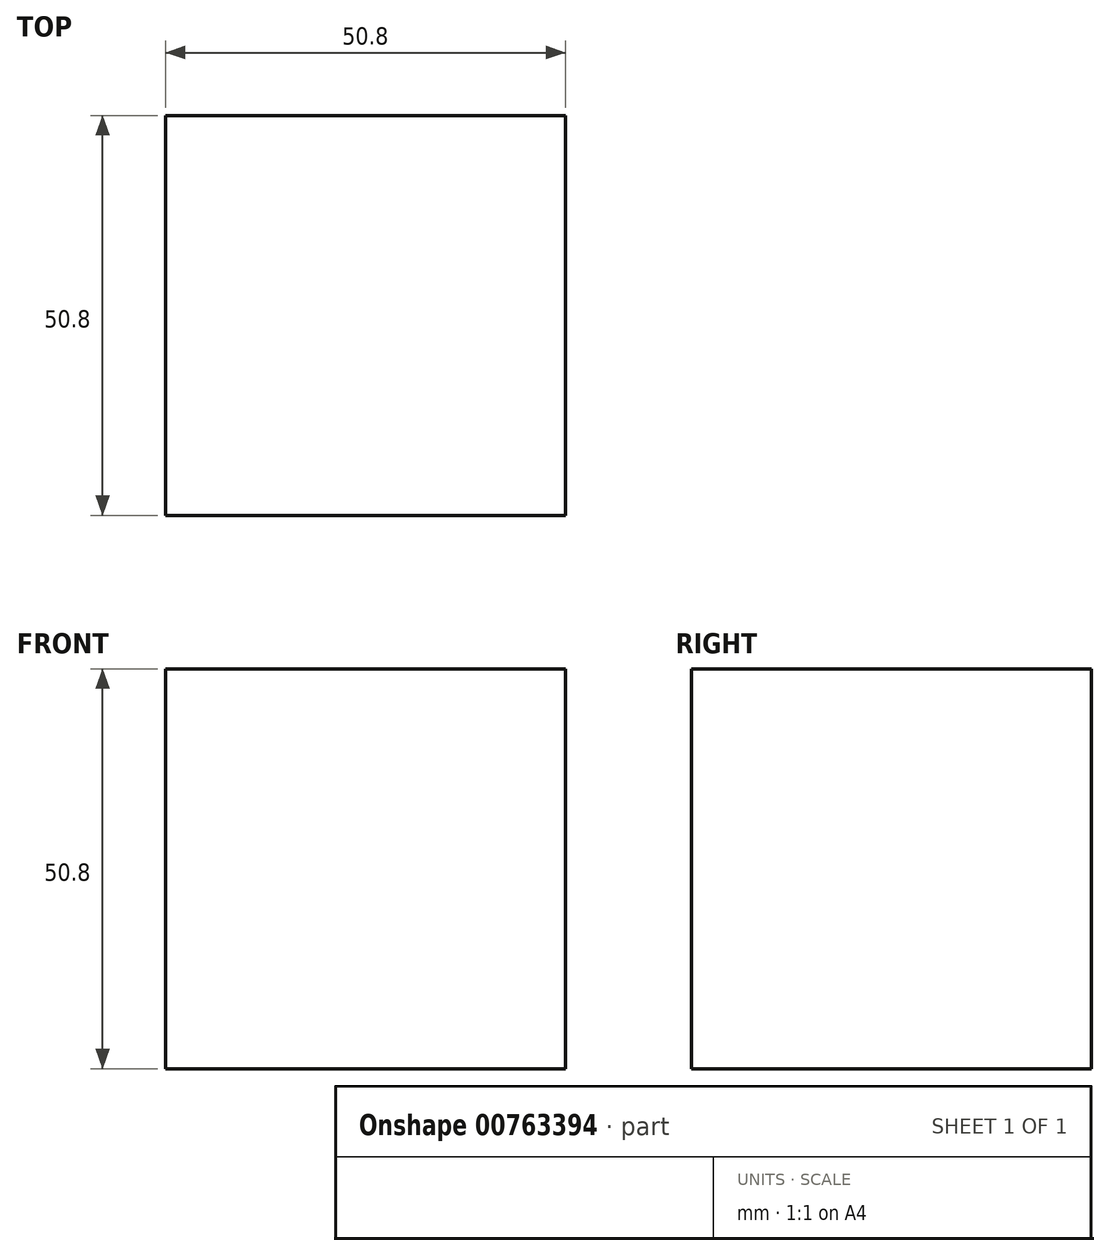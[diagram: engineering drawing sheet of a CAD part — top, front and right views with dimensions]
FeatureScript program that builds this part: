
annotation { "Feature Type Name" : "Feature", "Feature Type Description" : "" }
export const myFeature = defineFeature(function(context is Context, id is Id, definition is map)
    precondition{}
    {
        {
            var Q0;
            Q0=qCreatedBy(makeId("Front.planeOp"),FACE);
            var sketch = newSketch(context, id + "F0", { "sketchPlane" : qUnion([Q0])});
            skLineSegment(sketch, "E0.bottom", {"start": v(-25.4, 25.4) * mm, "end": v(25.4, 25.4) * mm});
            skLineSegment(sketch, "E0.top", {"start": v(-25.4, -25.4) * mm, "end": v(25.4, -25.4) * mm});
            skLineSegment(sketch, "E0.left", {"start": v(-25.4, 25.4) * mm, "end": v(-25.4, -25.4) * mm});
            skLineSegment(sketch, "E0.right", {"start": v(25.4, 25.4) * mm, "end": v(25.4, -25.4) * mm});
            skLineSegment(sketch, "E1", {"start": v(0, 0) * mm, "end": v(25.4, 0) * mm, "construction": true});
            skLineSegment(sketch, "E2", {"start": v(0, 0) * mm, "end": v(0, 25.4) * mm, "construction": true});
            skLineSegment(sketch, "E3", {"start": v(0, 0) * mm, "end": v(-25.4, 0) * mm});
            skLineSegment(sketch, "E4", {"start": v(0, 0) * mm, "end": v(0, -25.4) * mm});
            skSolve(sketch);
        }
        {
            var Q0;
            {var subQ1=sQuery(id+"F0.wireOp",EDGE,"E0.bottom");Q0=makeQuery(id+"F0.imprint","IMPRINT",FACE,{"disambiguationData":[TD([[makeQuery(id+"F0.imprint","IMPRINT",EDGE,{"derivedFrom":subQ1}),-1.0]])]});}
            var Q1;
            {var subQ5=sQuery(id+"F0.wireOp",EDGE,"E3");Q1=makeQuery(id+"F0.imprint","IMPRINT",FACE,{"disambiguationData":[TD([[makeQuery(id+"F0.imprint","IMPRINT",EDGE,{"derivedFrom":subQ5}),1.0]])]});}
            extrude(context, id + "F1", {"entities" : qUnion([Q0, Q1]), "depth" : 50.8 * mm, "offsetDistance" : 25.4 * mm});
        }
    });
